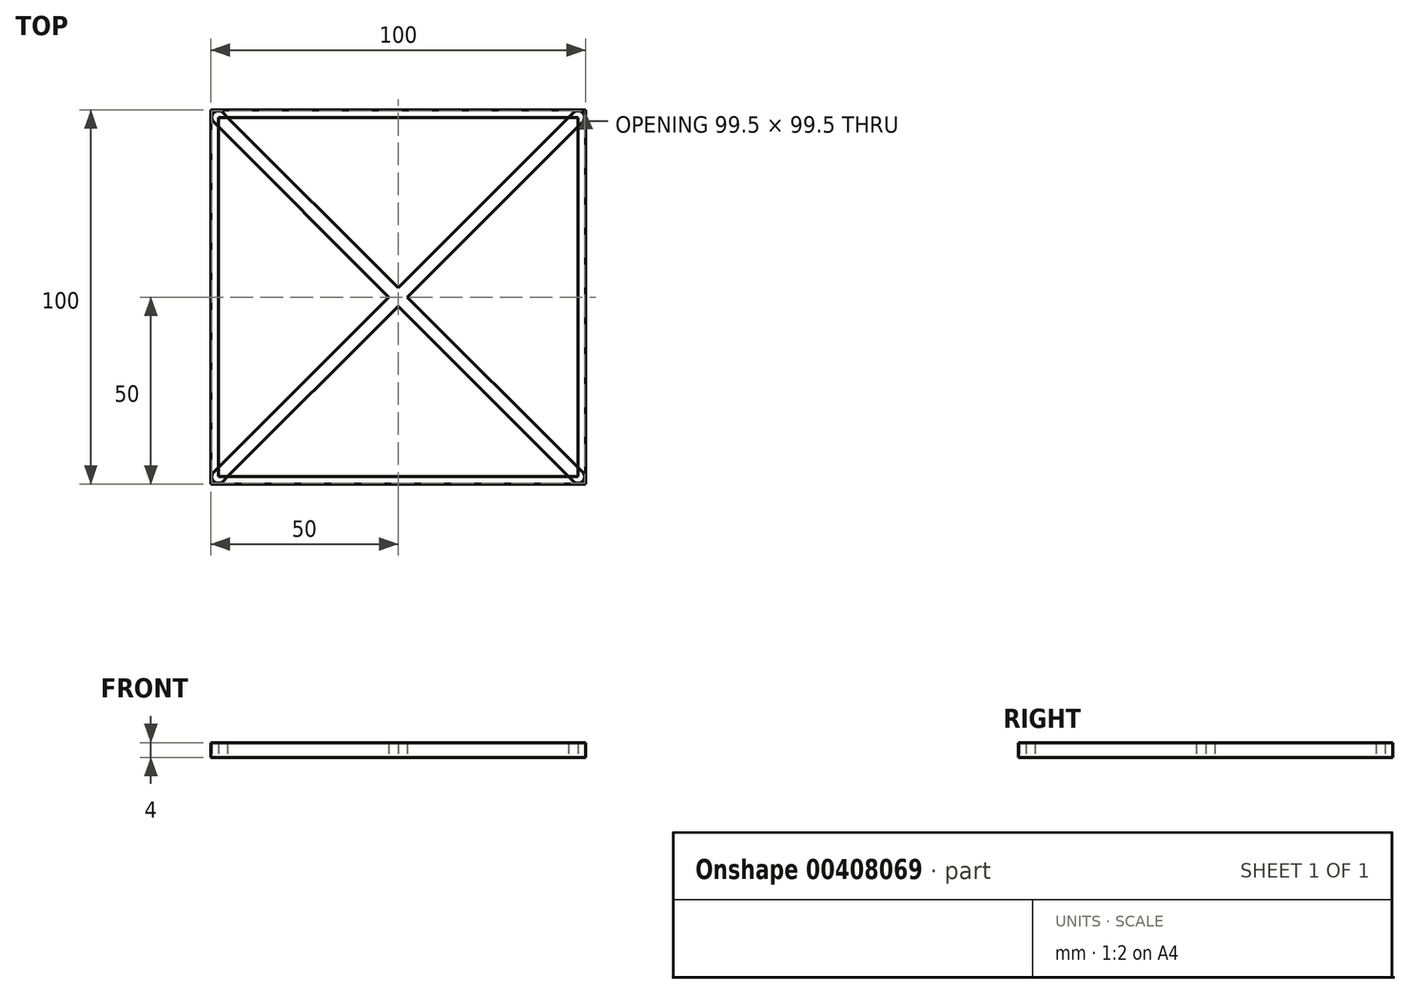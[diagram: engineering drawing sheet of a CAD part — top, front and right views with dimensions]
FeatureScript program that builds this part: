
annotation { "Feature Type Name" : "Feature", "Feature Type Description" : "" }
export const myFeature = defineFeature(function(context is Context, id is Id, definition is map)
    precondition{}
    {
        {
            var Q0;
            Q0=qCreatedBy(makeId("Top.planeOp"),FACE);
            var sketch = newSketch(context, id + "F0", { "sketchPlane" : qUnion([Q0])});
            skLineSegment(sketch, "E0.bottom", {"start": v(50, -50) * mm, "end": v(-50, -50) * mm});
            skLineSegment(sketch, "E0.top", {"start": v(50, 50) * mm, "end": v(-50, 50) * mm});
            skLineSegment(sketch, "E0.left", {"start": v(50, -50) * mm, "end": v(50, 50) * mm});
            skLineSegment(sketch, "E0.right", {"start": v(-50, -50) * mm, "end": v(-50, 50) * mm});
            skPoint(sketch, "E0.middle", {"position": v(0, 0) * mm});
            skLineSegment(sketch, "E1.0", {"start": v(-48, -48) * mm, "end": v(-48, 48) * mm});
            skLineSegment(sketch, "E1.1", {"start": v(48, -48) * mm, "end": v(-48, -48) * mm});
            skLineSegment(sketch, "E1.2", {"start": v(48, -48) * mm, "end": v(48, 48) * mm});
            skLineSegment(sketch, "E1.3", {"start": v(48, 48) * mm, "end": v(-48, 48) * mm});
            skLineSegment(sketch, "E2", {"start": v(-48, 48) * mm, "end": v(48, -48) * mm});
            skLineSegment(sketch, "E3", {"start": v(48, 48) * mm, "end": v(-48, -48) * mm});
            skArc(sketch, "E4.0.startCap", {"start": v(46.76, 49.24) * mm, "mid": v(49.24, 49.24) * mm, "end": v(49.24, 46.76) * mm});
            skArc(sketch, "E4.0.endCap", {"start": v(-46.76, -49.24) * mm, "mid": v(-49.24, -49.24) * mm, "end": v(-49.24, -46.76) * mm});
            skLineSegment(sketch, "E4.0.left", {"start": v(49.24, 46.76) * mm, "end": v(-46.76, -49.24) * mm});
            skLineSegment(sketch, "E4.0.right", {"start": v(46.76, 49.24) * mm, "end": v(-49.24, -46.76) * mm});
            skArc(sketch, "E4.1.startCap", {"start": v(-49.24, 46.76) * mm, "mid": v(-49.24, 49.24) * mm, "end": v(-46.76, 49.24) * mm});
            skArc(sketch, "E4.1.endCap", {"start": v(49.24, -46.76) * mm, "mid": v(49.24, -49.24) * mm, "end": v(46.76, -49.24) * mm});
            skLineSegment(sketch, "E4.1.left", {"start": v(-46.76, 49.24) * mm, "end": v(49.24, -46.76) * mm});
            skLineSegment(sketch, "E4.1.right", {"start": v(-49.24, 46.76) * mm, "end": v(46.76, -49.24) * mm});
            skSolve(sketch);
        }
        {
            var Q0;
            Q0=makeQuery(id+"F0.imprint","IMPRINT",FACE,{"disambiguationData":[TD([[makeQuery(id+"F0.imprint","IMPRINT",EDGE,{"derivedFrom":sQuery(id+"F0.wireOp",EDGE,"E0.bottom")}),-1.0]])]});
            var Q1;
            {var subQ0=sQuery(id+"F0.wireOp",EDGE,"E4.1.startCap");Q1=makeQuery(id+"F0.imprint","IMPRINT",FACE,{"disambiguationData":[TD([[makeQuery(id+"F0.imprint","IMPRINT",EDGE,{"derivedFrom":subQ0}),-1.0]])]});}
            var Q2;
            {var subQ0=sQuery(id+"F0.wireOp",EDGE,"E2");var subQ5=sQuery(id+"F0.wireOp",EDGE,"E4.0.right");var subQ6=makeQuery(id+"F0.imprint","INTERSECT",VERTEX,{"derivedFrom":[subQ0,subQ5]});Q2=makeQuery(id+"F0.imprint","IMPRINT",FACE,{"disambiguationData":[TD([[makeQuery(id+"F0.imprint","IMPRINT",EDGE,{"disambiguationData":[TD([[subQ6,-1.0]])],"derivedFrom":subQ5}),-1.0]])]});}
            var Q3;
            {var subQ0=sQuery(id+"F0.wireOp",EDGE,"E2");var subQ5=sQuery(id+"F0.wireOp",EDGE,"E4.0.right");var subQ6=makeQuery(id+"F0.imprint","INTERSECT",VERTEX,{"derivedFrom":[subQ0,subQ5]});Q3=makeQuery(id+"F0.imprint","IMPRINT",FACE,{"disambiguationData":[TD([[makeQuery(id+"F0.imprint","IMPRINT",EDGE,{"disambiguationData":[TD([[subQ6,1.0]])],"derivedFrom":subQ5}),-1.0]])]});}
            var Q4;
            {var subQ1=sQuery(id+"F0.wireOp",EDGE,"E1.3");var subQ3=sQuery(id+"F0.wireOp",EDGE,"E4.0.right");var subQ4=makeQuery(id+"F0.imprint","INTERSECT",VERTEX,{"derivedFrom":[subQ1,subQ3]});Q4=makeQuery(id+"F0.imprint","IMPRINT",FACE,{"disambiguationData":[TD([[makeQuery(id+"F0.imprint","IMPRINT",EDGE,{"disambiguationData":[TD([[subQ4,-1.0]])],"derivedFrom":subQ3}),1.0]])]});}
            var Q5;
            {var subQ1=sQuery(id+"F0.wireOp",EDGE,"E1.2");var subQ3=sQuery(id+"F0.wireOp",EDGE,"E4.0.left");var subQ4=makeQuery(id+"F0.imprint","INTERSECT",VERTEX,{"derivedFrom":[subQ1,subQ3]});Q5=makeQuery(id+"F0.imprint","IMPRINT",FACE,{"disambiguationData":[TD([[makeQuery(id+"F0.imprint","IMPRINT",EDGE,{"disambiguationData":[TD([[subQ4,-1.0]])],"derivedFrom":subQ3}),-1.0]])]});}
            var Q6;
            {var subQ0=sQuery(id+"F0.wireOp",EDGE,"E4.0.right");var subQ1=sQuery(id+"F0.wireOp",EDGE,"E2");var subQ2=makeQuery(id+"F0.imprint","INTERSECT",VERTEX,{"derivedFrom":[subQ1,subQ0]});Q6=makeQuery(id+"F0.imprint","IMPRINT",FACE,{"disambiguationData":[TD([[makeQuery(id+"F0.imprint","IMPRINT",EDGE,{"disambiguationData":[TD([[subQ2,-1.0]])],"derivedFrom":subQ1}),1.0]])]});}
            var Q7;
            {var subQ0=sQuery(id+"F0.wireOp",EDGE,"E3");var subQ1=sQuery(id+"F0.wireOp",EDGE,"E2");var subQ2=makeQuery(id+"F0.imprint","INTERSECT",VERTEX,{"derivedFrom":[subQ1,subQ0]});Q7=makeQuery(id+"F0.imprint","IMPRINT",FACE,{"disambiguationData":[TD([[makeQuery(id+"F0.imprint","IMPRINT",EDGE,{"disambiguationData":[TD([[subQ2,-1.0]])],"derivedFrom":subQ1}),1.0]])]});}
            var Q8;
            {var subQ0=sQuery(id+"F0.wireOp",EDGE,"E3");var subQ1=sQuery(id+"F0.wireOp",EDGE,"E2");var subQ2=makeQuery(id+"F0.imprint","INTERSECT",VERTEX,{"derivedFrom":[subQ1,subQ0]});Q8=makeQuery(id+"F0.imprint","IMPRINT",FACE,{"disambiguationData":[TD([[makeQuery(id+"F0.imprint","IMPRINT",EDGE,{"disambiguationData":[TD([[subQ2,-1.0]])],"derivedFrom":subQ1}),-1.0]])]});}
            var Q9;
            {var subQ0=sQuery(id+"F0.wireOp",EDGE,"E4.0.right");var subQ1=sQuery(id+"F0.wireOp",EDGE,"E2");var subQ2=makeQuery(id+"F0.imprint","INTERSECT",VERTEX,{"derivedFrom":[subQ1,subQ0]});Q9=makeQuery(id+"F0.imprint","IMPRINT",FACE,{"disambiguationData":[TD([[makeQuery(id+"F0.imprint","IMPRINT",EDGE,{"disambiguationData":[TD([[subQ2,-1.0]])],"derivedFrom":subQ1}),-1.0]])]});}
            var Q10;
            {var subQ1=sQuery(id+"F0.wireOp",EDGE,"E4.0.endCap");Q10=makeQuery(id+"F0.imprint","IMPRINT",FACE,{"disambiguationData":[TD([[makeQuery(id+"F0.imprint","IMPRINT",EDGE,{"derivedFrom":subQ1}),-1.0]])]});}
            var Q11;
            {var subQ0=sQuery(id+"F0.wireOp",EDGE,"E4.1.endCap");Q11=makeQuery(id+"F0.imprint","IMPRINT",FACE,{"disambiguationData":[TD([[makeQuery(id+"F0.imprint","IMPRINT",EDGE,{"derivedFrom":subQ0}),-1.0]])]});}
            var Q12;
            {var subQ1=sQuery(id+"F0.wireOp",EDGE,"E4.0.startCap");Q12=makeQuery(id+"F0.imprint","IMPRINT",FACE,{"disambiguationData":[TD([[makeQuery(id+"F0.imprint","IMPRINT",EDGE,{"derivedFrom":subQ1}),-1.0]])]});}
            var Q13;
            {var subQ1=sQuery(id+"F0.wireOp",EDGE,"E1.0");var subQ3=sQuery(id+"F0.wireOp",EDGE,"E4.0.right");var subQ4=makeQuery(id+"F0.imprint","INTERSECT",VERTEX,{"derivedFrom":[subQ1,subQ3]});Q13=makeQuery(id+"F0.imprint","IMPRINT",FACE,{"disambiguationData":[TD([[makeQuery(id+"F0.imprint","IMPRINT",EDGE,{"disambiguationData":[TD([[subQ4,1.0]])],"derivedFrom":subQ3}),1.0]])]});}
            var Q14;
            {var subQ0=sQuery(id+"F0.wireOp",EDGE,"E2");var subQ5=sQuery(id+"F0.wireOp",EDGE,"E4.0.left");var subQ6=makeQuery(id+"F0.imprint","INTERSECT",VERTEX,{"derivedFrom":[subQ0,subQ5]});Q14=makeQuery(id+"F0.imprint","IMPRINT",FACE,{"disambiguationData":[TD([[makeQuery(id+"F0.imprint","IMPRINT",EDGE,{"disambiguationData":[TD([[subQ6,-1.0]])],"derivedFrom":subQ5}),1.0]])]});}
            var Q15;
            {var subQ1=sQuery(id+"F0.wireOp",EDGE,"E1.1");var subQ3=sQuery(id+"F0.wireOp",EDGE,"E4.0.left");var subQ4=makeQuery(id+"F0.imprint","INTERSECT",VERTEX,{"derivedFrom":[subQ1,subQ3]});Q15=makeQuery(id+"F0.imprint","IMPRINT",FACE,{"disambiguationData":[TD([[makeQuery(id+"F0.imprint","IMPRINT",EDGE,{"disambiguationData":[TD([[subQ4,1.0]])],"derivedFrom":subQ3}),-1.0]])]});}
            var Q16;
            {var subQ0=sQuery(id+"F0.wireOp",EDGE,"E2");var subQ5=sQuery(id+"F0.wireOp",EDGE,"E4.0.left");var subQ6=makeQuery(id+"F0.imprint","INTERSECT",VERTEX,{"derivedFrom":[subQ0,subQ5]});Q16=makeQuery(id+"F0.imprint","IMPRINT",FACE,{"disambiguationData":[TD([[makeQuery(id+"F0.imprint","IMPRINT",EDGE,{"disambiguationData":[TD([[subQ6,1.0]])],"derivedFrom":subQ5}),1.0]])]});}
            extrude(context, id + "F1", {"entities" : qUnion([Q0, Q1, Q2, Q3, Q4, Q5, Q6, Q7, Q8, Q9, Q10, Q11, Q12, Q13, Q14, Q15, Q16]), "depth" : 4 * mm});
        }
    });
